# Revit family: Electronics_Desono_Biamp_Two-Way-Surface-Mount-Loudspeaker_MASK8F
name_source: partatom
category: Communication Devices
units: mm (PartAtom-declared; Revit-internal decimal feet)

## family parameters
Cut with Voids When Loaded = No
Host = Face
Maintain Annotation Orientation = No
OmniClass Number = 23.85.10.11.14.14.14
OmniClass Title = Loudspeakers
Part Type = Normal
Room Calculation Point = No
Round Connector Dimension = Use Diameter
Shared = No

## types (2) — shared parameters
Connector Description = Speakon™ connector; 40V 200 W 8Ω (800W peak)
Continuous Power Handling Nominal Impedance = 40V; 200W @ 8Ω (800W peak)
Default Elevation = 4' - 0"
Depth = 0' - 10"
Description = Desono™ MASK8F Two-Way 8-Inch Surface Mount Loudspeaker
Height = 1' - 4"
Input Connection = (2x) Speakon™ connectors; (2x) 5-way binding posts
Manufacturer = Biamp
Mounting Provisions = U-bracket; pole-mount adapter
Nominal Beamwidth  (H x V) = 100° x 100°
Nominal Maximum SPL @ 1m = Peak - 116dB; Continuous - 110dB
Nominal Sensitivity @ 1m = 1W - 87dB; 2.83V - 87dB
Operating Environment = Indoor
Operating Mode = Passive
Operating Range (-10dB) = 53 Hz to 22 kHz
Product Documentation Link = https://downloads.biamp.com
Product Page URL = https://www.biamp.com
Product data url = https://www.bimobject.com
Protection = 2-step self-resetting protection
Recommended Amplifers = 200W - 400W @ 8Ω (40V - 57V)
Shipping Weight = 24.70 lb
Transducers = LF 1 x 8 (203 mm) coated paper cone HF 1 x 1 (25 mm) soft dome
URL = https://www.biamp.com
Weight = 19.80 lb
Width = 0' - 10"

## per-type parameters (varying)
| type | Bracket Material | Grill Material | Housing Material |
| MASK8F W | Biamp - Metal - White | Biamp - Plastic - White(Grid) | Biamp - Plastic - White |
| MASK8F B | Biamp - Metal - Black | Biamp - Plastic - Black(Grid) | Biamp - Plastic - Black |

note: column(s) folded — value = type name in every type: Model

## geometry (parser evidence)
native form markers: Sweep x4
no freeform markers — native parametric forms only
